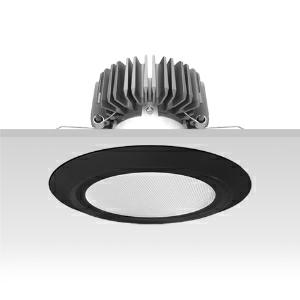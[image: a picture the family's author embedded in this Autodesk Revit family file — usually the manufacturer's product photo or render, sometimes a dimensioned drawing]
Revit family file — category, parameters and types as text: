
# Revit family: 3f_filippi_-_3f_reno_bianco_ampio_3f_filippi_-_30650_a01038_-_3f_reno_200_wh_2000-930_ep_wide___vs_bk_b3b4
name_source: partatom
category: Lighting Fixtures
units: mm (PartAtom-declared; Revit-internal decimal feet)

## family parameters
Cut with Voids When Loaded = No
Host = Face
Light Source = No
Part Type = Normal
Room Calculation Point = No
Round Connector Dimension = Use Diameter
Shared = No

## types (1)
- 3F Filippi - 3F Reno Bianco Ampio (1 x LED, 1650 lm, 25 W, 3000 K)
    Apparent Load = 25 VA
    Approval mark = ENEC
    CIE Flux Codes = 75 94 99 100 100
    Color Rendering = 90
    Color Temperature = 3000 K
    Control Gear = Electronic ballast
    Default Elevation = 1800 mm
    Description = ILLUMINOTECHNICAL
Luminous efficiency 100% (DLOR 100%, ULOR 0%).
Initial luminous flux of the luminaire 1650 lm.
Emergency luminaire luminous flux BLF 16.7%.
Direct symmetric wide distribution.
Installation Interdistance Transv.D = 1.16 x hu - Long.D = 1.14 x hu.
Average luminance <3000 cd/m² for radial angles >65°.
Tabular UGR (CIE 117 - 4H-8H; S=0.25H; 70/50/20): RUG 20.3 - 20.2.
Beam angle: 74° - 74°.
Luminous efficacy 66 lm/W.
Lifetime (L90/B10): 30000 h. (tq+25°C)
Lifetime (L85/B10): 50000 h. (tq+25°C)
Lifetime (L70/B10): 80000 h. (tq+25°C)
Sudden decreased luminous flux after 50000 hours: 0% (C0).
Photobiological safety in compliance with IEC/TR 62778: RG0 risk exempt, (IEC 62471).
In compliance with IEC/EN 62722-2-1 - IEC/EN 62717 standards.

SOURCE
Compact LED module 2000/930.
Energy efficiency class (UE 2019/2020 - UE 2019/2015): E.
CIE 13.3 Colour rendering index: CRI >90 (R9 >50%).
IES TM-30 Fidelity Index: Rf = 92 Rg = 101.
CCT nominal colour temperature 3000 K.
Colour initial tolerance (MacAdam): SDCM 3.
Zhaga Book 3 compliant.

MECHANICAL
Passive heat dissipator in die-casting aluminium, oversized, for optimum thermal management of the LED module.
Parabolic element with graduated/concentric rings in white polycarbonate.
Transparent external lens with glossy and satin differentiated surfaces, with a cooling and anti-insect system in methacrylate (PMMA).
Fastening spring clips in stainless steel.
Dimensions: diameter 226 mm, height 146 mm. Weight 1.685 kg.
IP44 protection degree for exposed part, IP20 for recessed part.
Mechanical strength to impacts IK06 (1 joule).
Glow-wire test resistance 650°C.

ELECTRICAL
Wiring on a separate unit.
Halogen Free electronic wiring 230V-50/60Hz, power factor 0.90, THD <25%, constant output current, SELV, class II, 1 driver.
Power of the luminaire 25 W.
CE - IEC 60598-1 - EN 60598-1.
EP maintained emergency wiring on board, 1h duration, 24h recharge; compliant with EN 60598-2-22, excluding high risk areas.
SAFE FLICKER: PstLM=<1 and SVM=<0.4 (IEC TR 61547-1 and IEC TR 63158), to ensure a more comfortable and safe light.
Ambient temperature from +5°C to +25°C.
Temperature class T6 max 85°C.
Relative humidity UR: <85%.

INSTALLATION
Pull-up recessed fitting.
False ceiling carving: 200 mm.
All accessories dedicated to this product are available on the Catalog and on our website www.3F-Filippi.com.

ACCESSORIES
A01038 - Anti-glare microprismatic VS moulded glass, tempered, not flammable, locked and in line with the trim, in black polycarbonate.

APPLICATIONS
Environments: architectural, commercial, exhibition areas, transit areas, corridors, shops, display windows, service areas.
In false ceilings with narrow voids.

WARNING
Luminaire designed for disposal/recycling at end-of-life.
Replaceable (LED only) light source by a professional. Replaceable control gear by a professional.
    Height = 0 mm  [stored 0 ft]
    Lamp = 1 x LED
    Lamp Light Flux = 1650 lm
    Lamp Power = 25 W
    Lamp count = 1
    Length = 226 mm
    Lifetime = 50000 h
    Luminous efficacy = 66 lm/W
    Manufacturer = 3F Filippi
    ModVariant = No
    Model = 3F Filippi - 30650+A01038 - 3F Reno 200 WH 2000-930 EP WIDE + VS BK
    Mounting Place = Ceiling
    Mounting Type = Recessed
    Number of Poles = 1
    OnlyDefault = Yes
    Power Factor = 1
    Product Name = 3F Filippi - 3F Reno Bianco Ampio
    Product group = recessed luminaire
    ProductGroupID = 4
    Protection Class = Protection class II
    Protection Degree = IP 20
    RLX_Detail_Level = 1
    RLX_Emergency_Light_Flux = 0 lm
    RLX_Emergency_Type = 0
    RLX_Emergency_Type_DB = No
    RlxData = <blob elided: 97209 chars, md5=0c91355f>
    Socket = socket
    Standby Power = 0 W
    System Light Flux = 1650 lm
    System Power = 25 W
    Type Comments = Product without accessories
    Type Image = 3ffilippi_3f_reno_200_bk_vs_smp.jpg
    URL = http://relux.com
    VarID = ---
    Voltage = 0 V
    Weight = 0.00 kg
    Width = 0 mm  [stored 0 ft]

note: [stored X ft] marks values corroborated as IEEE doubles in the binary element streams (Revit-internal decimal feet)

## geometry (parser evidence)
native form markers: Blend x4, Sweep x9
no freeform markers — native parametric forms only
